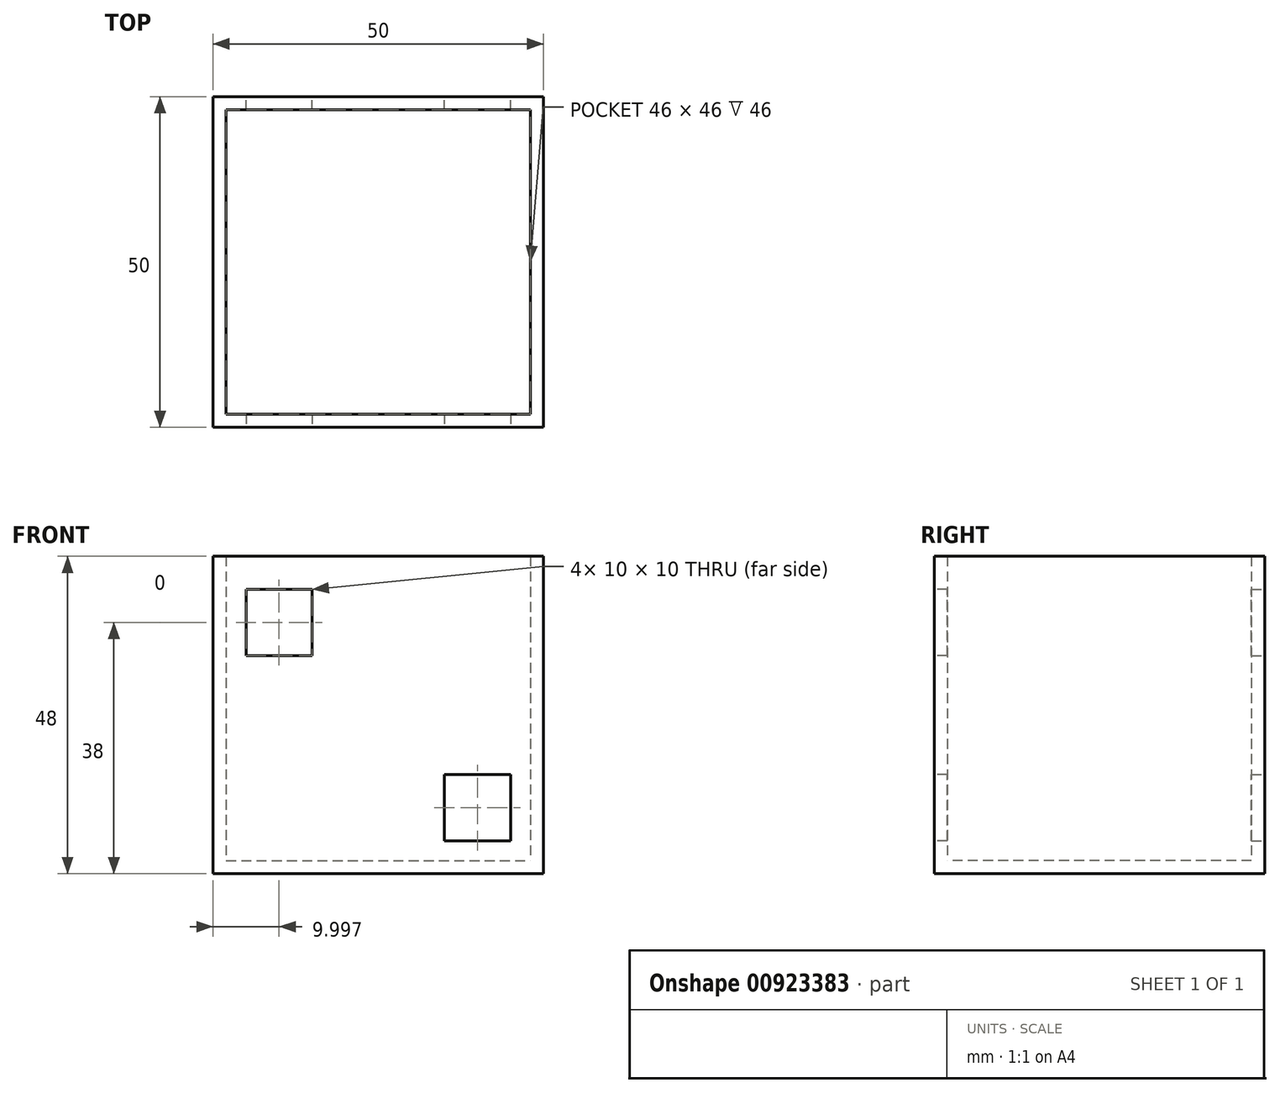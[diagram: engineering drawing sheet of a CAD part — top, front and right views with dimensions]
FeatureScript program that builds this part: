
annotation { "Feature Type Name" : "Feature", "Feature Type Description" : "" }
export const myFeature = defineFeature(function(context is Context, id is Id, definition is map)
    precondition{}
    {
        {
            var Q0;
            Q0=qCreatedBy(makeId("Top.planeOp"),FACE);
            var sketch = newSketch(context, id + "F0", { "sketchPlane" : qUnion([Q0])});
            skLineSegment(sketch, "E0.bottom", {"start": v(-26.76, 30.55) * mm, "end": v(23.24, 30.55) * mm});
            skLineSegment(sketch, "E0.top", {"start": v(-26.76, -19.45) * mm, "end": v(23.24, -19.45) * mm});
            skLineSegment(sketch, "E0.left", {"start": v(-26.76, 30.55) * mm, "end": v(-26.76, -19.45) * mm});
            skLineSegment(sketch, "E0.right", {"start": v(23.24, 30.55) * mm, "end": v(23.24, -19.45) * mm});
            skSolve(sketch);
        }
        {
            var Q0;
            Q0=makeQuery(id+"F0.imprint","IMPRINT",FACE,{"disambiguationData":[TD([[makeQuery(id+"F0.imprint","IMPRINT",EDGE,{"derivedFrom":sQuery(id+"F0.wireOp",EDGE,"E0.bottom")}),-1.0]])]});
            extrude(context, id + "F1", {"entities" : qUnion([Q0]), "depth" : 48 * mm, "offsetDistance" : 25.4 * mm});
        }
        {
            var Q0;
            Q0=makeQuery(id+"F1.opExtrude","CAP_FACE",FACE,{"disambiguationData":[OSD([sQuery(id+"F0.wireOp",EDGE,"E0.bottom"),sQuery(id+"F0.wireOp",EDGE,"E0.top"),sQuery(id+"F0.wireOp",EDGE,"E0.left"),sQuery(id+"F0.wireOp",EDGE,"E0.right")])],"isStart":false});
            shell(context, id + "F2", {"entities" : qUnion([Q0]), "thickness" : 2 * mm});
        }
        {
            var Q0;
            Q0=makeQuery(id+"F1.opExtrude","SWEPT_FACE",FACE,{"disambiguationData":[OSD([sQuery(id+"F0.wireOp",EDGE,"E0.top")])]});
            var sketch = newSketch(context, id + "F3", { "sketchPlane" : qUnion([Q0])});
            skLineSegment(sketch, "E1.bottom", {"start": v(-11.76, 33) * mm, "end": v(-21.76, 33) * mm});
            skLineSegment(sketch, "E1.top", {"start": v(-11.76, 43) * mm, "end": v(-21.76, 43) * mm});
            skLineSegment(sketch, "E1.left", {"start": v(-11.76, 33) * mm, "end": v(-11.76, 43) * mm});
            skLineSegment(sketch, "E1.right", {"start": v(-21.76, 33) * mm, "end": v(-21.76, 43) * mm});
            skPoint(sketch, "E1.middle", {"position": v(-16.76, 38) * mm});
            skLineSegment(sketch, "E2.bottom", {"start": v(18.24, 5) * mm, "end": v(8.24, 5) * mm});
            skLineSegment(sketch, "E2.top", {"start": v(18.24, 15) * mm, "end": v(8.24, 15) * mm});
            skLineSegment(sketch, "E2.left", {"start": v(18.24, 5) * mm, "end": v(18.24, 15) * mm});
            skLineSegment(sketch, "E2.right", {"start": v(8.24, 5) * mm, "end": v(8.24, 15) * mm});
            skPoint(sketch, "E2.middle", {"position": v(13.24, 10) * mm});
            skSolve(sketch);
        }
        {
            var Q0;
            Q0=makeQuery(id+"F1.opExtrude","SWEPT_FACE",FACE,{"disambiguationData":[OSD([sQuery(id+"F0.wireOp",EDGE,"E0.bottom")])]});
            var sketch = newSketch(context, id + "F4", { "sketchPlane" : qUnion([Q0])});
            skLineSegment(sketch, "E3.bottom", {"start": v(21.76, 33) * mm, "end": v(11.76, 33) * mm});
            skLineSegment(sketch, "E3.top", {"start": v(21.76, 43) * mm, "end": v(11.76, 43) * mm});
            skLineSegment(sketch, "E3.left", {"start": v(21.76, 33) * mm, "end": v(21.76, 43) * mm});
            skLineSegment(sketch, "E3.right", {"start": v(11.76, 33) * mm, "end": v(11.76, 43) * mm});
            skPoint(sketch, "E3.middle", {"position": v(16.76, 38) * mm});
            skLineSegment(sketch, "E4.bottom", {"start": v(-8.24, 5) * mm, "end": v(-18.24, 5) * mm});
            skLineSegment(sketch, "E4.top", {"start": v(-8.24, 15) * mm, "end": v(-18.24, 15) * mm});
            skLineSegment(sketch, "E4.left", {"start": v(-8.24, 5) * mm, "end": v(-8.24, 15) * mm});
            skLineSegment(sketch, "E4.right", {"start": v(-18.24, 5) * mm, "end": v(-18.24, 15) * mm});
            skPoint(sketch, "E4.middle", {"position": v(-13.24, 10) * mm});
            skSolve(sketch);
        }
        {
            var Q0;
            Q0=makeQuery(id+"F3.imprint","IMPRINT",FACE,{"disambiguationData":[TD([[makeQuery(id+"F3.imprint","IMPRINT",EDGE,{"derivedFrom":sQuery(id+"F3.wireOp",EDGE,"E1.bottom")}),-1.0]])]});
            var Q1;
            Q1=makeQuery(id+"F3.imprint","IMPRINT",FACE,{"disambiguationData":[TD([[makeQuery(id+"F3.imprint","IMPRINT",EDGE,{"derivedFrom":sQuery(id+"F3.wireOp",EDGE,"E2.bottom")}),-1.0]])]});
            extrude(context, id + "F5", {"entities" : qUnion([Q0, Q1]), "operationType" : NewBodyOperationType.REMOVE, "oppositeDirection" : true, "depth" : 2 * mm, "offsetDistance" : 25.4 * mm});
        }
        {
            var Q0;
            Q0=makeQuery(id+"F4.imprint","IMPRINT",FACE,{"disambiguationData":[TD([[makeQuery(id+"F4.imprint","IMPRINT",EDGE,{"derivedFrom":sQuery(id+"F4.wireOp",EDGE,"E3.bottom")}),-1.0]])]});
            var Q1;
            Q1=makeQuery(id+"F4.imprint","IMPRINT",FACE,{"disambiguationData":[TD([[makeQuery(id+"F4.imprint","IMPRINT",EDGE,{"derivedFrom":sQuery(id+"F4.wireOp",EDGE,"E4.bottom")}),-1.0]])]});
            extrude(context, id + "F6", {"entities" : qUnion([Q0, Q1]), "operationType" : NewBodyOperationType.REMOVE, "oppositeDirection" : true, "depth" : 2 * mm, "offsetDistance" : 25.4 * mm});
        }
    });
